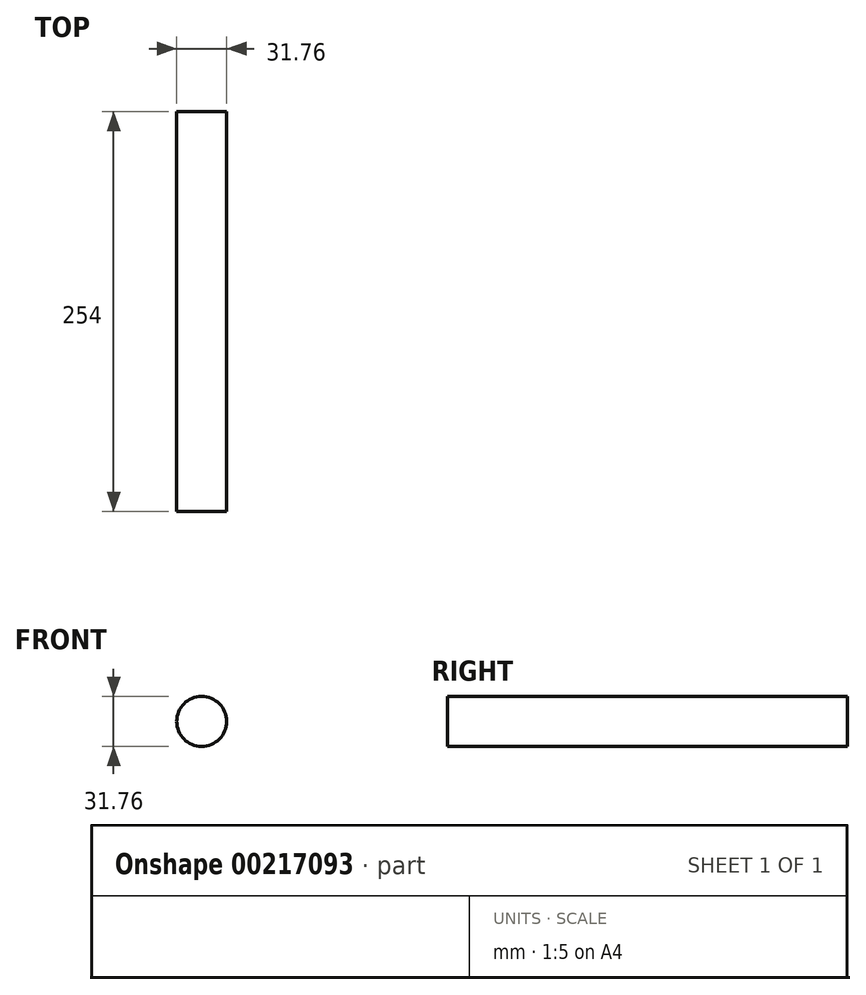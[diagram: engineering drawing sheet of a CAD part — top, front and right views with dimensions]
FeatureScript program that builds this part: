
annotation { "Feature Type Name" : "Feature", "Feature Type Description" : "" }
export const myFeature = defineFeature(function(context is Context, id is Id, definition is map)
    precondition{}
    {
        {
            var Q0;
            Q0=qCreatedBy(makeId("Front.planeOp"),FACE);
            var sketch = newSketch(context, id + "F0", { "sketchPlane" : qUnion([Q0])});
            skCircle(sketch, "E0", {"center": v(0, 0) * mm, "radius": 15.88 * mm});
            skSolve(sketch);
        }
        {
            var Q0;
            Q0 = qSketchRegion(id + "F0", true);
            extrude(context, id + "F1", {"entities" : qUnion([Q0]), "depth" : 254 * mm});
        }
    });
